# Revit family: avt-vk
name_source: partatom
category: Mechanical Equipment
revit_build: Autodesk Revit 2018 (Build: 20170223_1515(x64)
units: mm (PartAtom-declared; Revit-internal decimal feet)

## family parameters
Always vertical = Yes
Cut with Voids When Loaded = No
OmniClass Number = 23.75.00.00
OmniClass Title = Climate Control (HVAC)
Part Type = Normal
Room Calculation Point = No
Round Connector Dimension = Use Radius
Shared = No
Work Plane-Based = No

## types (7) — shared parameters
Classification.Uniclass.Pr.Description = Fans
Classification.Uniclass.Pr.Number = Pr_65_67_29
Fan Unit = No
Fax Number = +44(0)2920-858-222
I&M Manual = http://nuaire.info
IFCExportAs = IfcFanType
Manufacturer = Nuaire
Manufacturer Name = Nuaire
Maximum Ambient Temperature = 40 °C
OmniClass Number = 23-33 31 19
OmniClass Title = Fans
Postcode = CF83 1NA
Revit Family Last Revised = 23/07/2020
Telephone Number = +44(0)2920-858-200
Type Comments = 1
URL = http://www.nuaire.co.uk
VAT Registration Number = 877308
Warranty Period = 1 Years
Weatherproof or Internal Only = Internal
Weight = 0.00 kg

## per-type parameters (varying)
| type | Description | Unit Description | bracket_size | unit_length | unit_width |
| AVT1-VK | Vertical Mounting Kit for the AVT1 | Vertical Mounting Kit for the AVT1 | avt-vk_bracket : 1 | 927 mm  [stored 3.04134 ft] | 545 mm  [stored 1.78806 ft] |
| AVT2-VK | Vertical Mounting Kit for the AVT2 | Vertical Mounting Kit for the AVT2 | avt-vk_bracket : 2 | 968 mm  [stored 3.17585 ft] | 545 mm  [stored 1.78806 ft] |
| AVT3-VK | Vertical Mounting Kit for the AVT3 | Vertical Mounting Kit for the AVT3 | avt-vk_bracket : 3 | 1186 mm  [stored 3.89108 ft] | 682 mm |
| AVT4-VK | Vertical Mounting Kit for the AVT4 | Vertical Mounting Kit for the AVT4 | avt-vk_bracket : 4 | 1229 mm  [stored 4.03215 ft] | 682 mm |
| AVT4L-VK | Vertical Mounting Kit for the AVT4L | Vertical Mounting Kit for the AVT4L | avt-vk_bracket : 4 | 1531 mm  [stored 5.02297 ft] | 828 mm  [stored 2.71654 ft] |
| AVT5-VK | Vertical Mounting Kit for the AVT5 | Vertical Mounting Kit for the AVT5 | avt-vk_bracket : 5 | 1531 mm  [stored 5.02297 ft] | 828 mm  [stored 2.71654 ft] |
| AVT6-VK | Vertical Mounting Kit for the AVT6 | Vertical Mounting Kit for the AVT6 | avt-vk_bracket : 6 | 1531 mm  [stored 5.02297 ft] | 828 mm  [stored 2.71654 ft] |

note: column(s) folded — value = type name in every type: Model, Nuaire Model No, Supplier Part No

note: [stored X ft] marks values corroborated as IEEE doubles in the binary element streams (Revit-internal decimal feet)

## geometry (parser evidence)
native form markers: Blend x14, Sweep x4
no freeform markers — native parametric forms only
